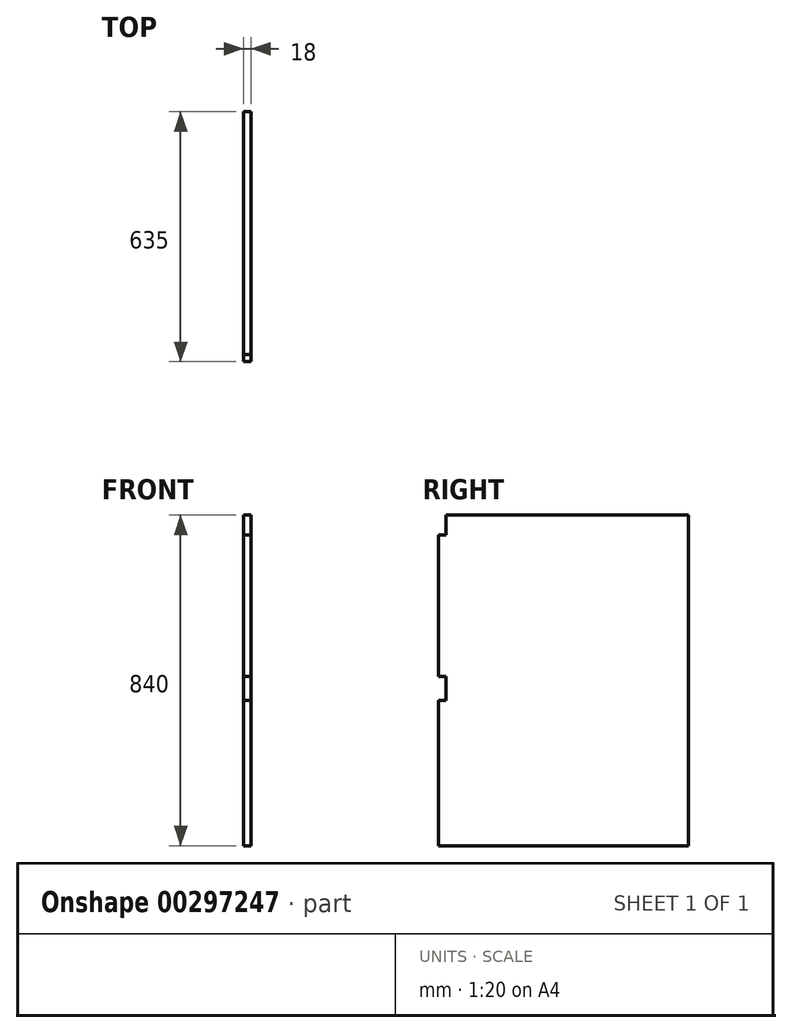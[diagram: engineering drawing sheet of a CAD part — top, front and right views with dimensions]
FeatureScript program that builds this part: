
annotation { "Feature Type Name" : "Feature", "Feature Type Description" : "" }
export const myFeature = defineFeature(function(context is Context, id is Id, definition is map)
    precondition{}
    {
        {
            var Q0;
            Q0=qCreatedBy(makeId("Right.planeOp"),FACE);
            var sketch = newSketch(context, id + "F0", { "sketchPlane" : qUnion([Q0])});
            skLineSegment(sketch, "E0.bottom", {"start": v(317.5, 420) * mm, "end": v(-317.5, 420) * mm});
            skLineSegment(sketch, "E0.top", {"start": v(317.5, -420) * mm, "end": v(-317.5, -420) * mm});
            skLineSegment(sketch, "E0.left", {"start": v(317.5, 420) * mm, "end": v(317.5, -420) * mm});
            skLineSegment(sketch, "E0.right", {"start": v(-317.5, 420) * mm, "end": v(-317.5, -420) * mm});
            skPoint(sketch, "E0.middle", {"position": v(0, 0) * mm});
            skSolve(sketch);
        }
        {
            var Q0;
            Q0=qSketchRegion(id+"F0",true);
            extrude(context, id + "F1", {"entities" : qUnion([Q0]), "depth" : 18 * mm});
        }
        {
            var Q0;
            Q0=makeQuery(id+"F1.opExtrude","CAP_FACE",FACE,{"disambiguationData":[OSD([sQuery(id+"F0.wireOp",EDGE,"E0.bottom"),sQuery(id+"F0.wireOp",EDGE,"E0.top"),sQuery(id+"F0.wireOp",EDGE,"E0.left"),sQuery(id+"F0.wireOp",EDGE,"E0.right")])],"isStart":false});
            var sketch = newSketch(context, id + "F2", { "sketchPlane" : qUnion([Q0])});
            skLineSegment(sketch, "E1.bottom", {"start": v(-317.5, 420) * mm, "end": v(-299.5, 420) * mm});
            skLineSegment(sketch, "E1.top", {"start": v(-317.5, 370) * mm, "end": v(-299.5, 370) * mm});
            skLineSegment(sketch, "E1.left", {"start": v(-317.5, 420) * mm, "end": v(-317.5, 370) * mm});
            skLineSegment(sketch, "E1.right", {"start": v(-299.5, 420) * mm, "end": v(-299.5, 370) * mm});
            skLineSegment(sketch, "E2.bottom", {"start": v(-317.5, -50) * mm, "end": v(-299.5, -50) * mm});
            skLineSegment(sketch, "E2.top", {"start": v(-317.5, 10) * mm, "end": v(-299.5, 10) * mm});
            skLineSegment(sketch, "E2.left", {"start": v(-317.5, -50) * mm, "end": v(-317.5, 10) * mm});
            skLineSegment(sketch, "E2.right", {"start": v(-299.5, -50) * mm, "end": v(-299.5, 10) * mm});
            skSolve(sketch);
        }
        {
            var Q0;
            Q0=qSketchRegion(id+"F2",true);
            extrude(context, id + "F3", {"entities" : qUnion([Q0]), "operationType" : NewBodyOperationType.REMOVE, "oppositeDirection" : true, "depth" : 18 * mm});
        }
    });
